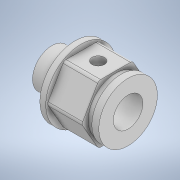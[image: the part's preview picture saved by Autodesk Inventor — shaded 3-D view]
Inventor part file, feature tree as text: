
AUTODESK INVENTOR PART (.ipt)
format: ipt  version: 2020 (Build 240168000, 168)  size: 193,536 bytes
history: native  units: mm
features: sketch x9, extrude x7, fillet x3
ambient origin geometry x8: Origin, YZ Plane, XZ Plane, XY Plane, X Axis, Y Axis, Z Axis, Center Point
bodies: Solid1 (feature_tree)
feature tree (19):
  extrude  "Extrusion1"  Depth=1.28mm TaperAngle=0.0deg
  extrude  "Extrusion2"  Depth=11.854mm
  extrude  "Extrusion3"  Depth=1.5mm TaperAngle=0.0deg
  extrude  "Extrusion4"  Depth=0.75mm
  fillet  "Fillet1"  Radius=2.705mm
  fillet  "Fillet2"  Radius=6.5mm
  sketch  "Sketch5"  dims[d15=6.4mm d16=11.75mm d17=0.0mm]
  extrude  "Extrusion5"  Depth=11.75mm TaperAngle=0.0deg
  sketch  "Sketch7"  dims[d21=2.0mm]
  sketch  "Sketch8"
  extrude  "Extrusion6"  Depth=5.0mm TaperAngle=0.0deg
  extrude  "Extrusion7"  [1 undecoded]
  fillet  "Fillet3"  [1 undecoded]
  sketch  "Sketch1"  dims[d0=15.197mm d1=1.28mm d2=0.0mm]
  sketch  "Sketch2"  dims[d3=7.5mm d4=0.0mm d5=11.854mm]
  sketch  "Sketch3"  dims[d6=1.22mm d7=0.0mm d8=1.5mm d9=0.0mm]
  sketch  "Sketch4"  dims[d10=0.75mm d11=0.75mm d12=2.705mm d13=6.5mm d14=0.0mm]
  sketch  "Sketch6"  dims[d18=8.4mm d19=5.0mm d20=0.0mm]
  sketch  "Sketch9"
note: 2 required parameter values undecoded (feature->parameter linkage not recoverable at this tier; creation-order binding heuristic only, values carry confidence <= 0.55)
